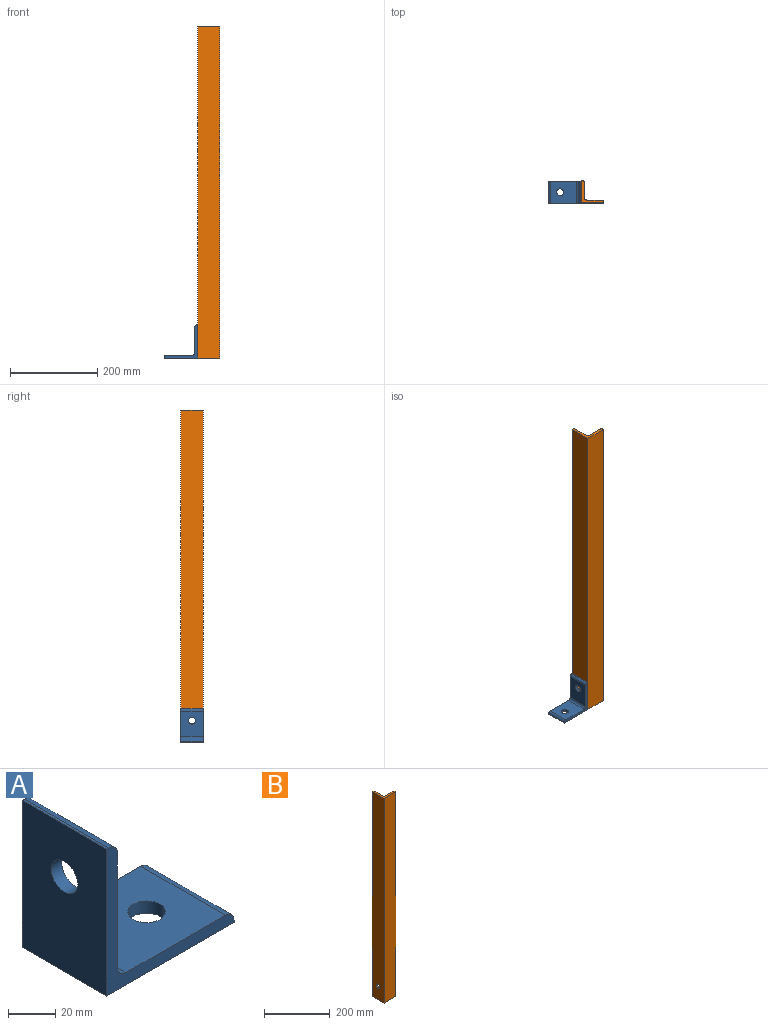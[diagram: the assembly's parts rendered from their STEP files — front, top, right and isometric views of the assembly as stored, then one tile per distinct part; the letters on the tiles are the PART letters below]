
ASSEMBLY  parts=2 mates=1
PART A: 13 faces, bbox 76.2x50.8x76.2 mm
  f0: plane 59.69x50.8mm, normal (0,0,1), area 2834.3mm2, adj f6,f7,f8,f10,f12
  f1: plane 59.61x50.8mm, normal (1,0,0), area 2830.4mm2, adj f6,f7,f8,f9,f11
  f2: plane 50.8x1.27mm, normal (0,0,1), area 64.5mm2, adj f3,f6,f7,f9
  f3: plane 76.2x50.8mm, normal (-1,0,0), area 3673mm2, adj f2,f4,f6,f7,f11
  f4: plane 76.2x50.8mm, normal (0,0,-1), area 3673mm2, adj f3,f5,f6,f7,f12
  f5: plane 50.8x1.35mm, normal (1,0,0), area 68.4mm2, adj f4,f6,f7,f10
  f6: plane 76.2x76.2mm, normal (0,-1,0), area 927.2mm2, adj f0,f1,f2,f3,f4,f5,f8,f9
  f7: plane 76.2x76.2mm, normal (0,1,0), area 927.2mm2, adj f0,f1,f2,f3,f4,f5,f8,f9
  f8: cylinder r=5.08mm len=50.8mm, axis (0,-1,0), area 405.4mm2, adj f0,f1,f6,f7
  f9: cylinder r=5.08mm len=50.8mm, axis (0,1,0), area 405.4mm2, adj f1,f2,f6,f7
  f10: cylinder r=5.08mm len=50.8mm, axis (0,1,0), area 405.4mm2, adj f0,f5,f6,f7
  f11: cylinder r=7.94mm len=15.88mm, axis (-1,0,0), area 316.7mm2, adj f1,f3
  f12: cylinder r=7.94mm len=15.88mm, axis (0,0,-1), area 320.5mm2, adj f0,f4
PART B: 12 faces, bbox 50.8x50.8x762 mm
  f0: plane 762x34.29mm, normal (0,1,0), area 26129mm2, adj f6,f7,f8,f10
  f1: plane 762x34.29mm, normal (1,0,0), area 25931mm2, adj f6,f7,f8,f9,f11
  f2: plane 762x1.27mm, normal (0,1,0), area 967.7mm2, adj f3,f6,f7,f9
  f3: plane 762x50.8mm, normal (-1,0,0), area 38511.7mm2, adj f2,f4,f6,f7,f11
  f4: plane 762x50.8mm, normal (0,-1,0), area 38709.6mm2, adj f3,f5,f6,f7
  f5: plane 762x1.27mm, normal (1,0,0), area 967.7mm2, adj f4,f6,f7,f10
  f6: plane 50.8x50.8mm, normal (0,0,1), area 599.3mm2, adj f0,f1,f2,f3,f4,f5,f8,f9
  f7: plane 50.8x50.8mm, normal (0,0,-1), area 599.3mm2, adj f0,f1,f2,f3,f4,f5,f8,f9
  f8: cylinder r=5.08mm len=762mm, axis (0,0,1), area 6080.5mm2, adj f0,f1,f6,f7
  f9: cylinder r=5.08mm len=762mm, axis (0,0,-1), area 6080.5mm2, adj f1,f2,f6,f7
  f10: cylinder r=5.08mm len=762mm, axis (0,0,-1), area 6080.5mm2, adj f0,f5,f6,f7
  f11: cylinder r=7.94mm len=15.88mm, axis (-1,0,0), area 316.7mm2, adj f1,f3
PLACE A rot(axis=(0,0,1),180deg) t=(-351.95,-77.34,-217.05)mm
PLACE B t=(-288.45,-77.34,125.85)mm
MATE fastened A.f11 <-> B.f11  axis (1,0,0) through (-313.85,-77.34,-205.94)mm
